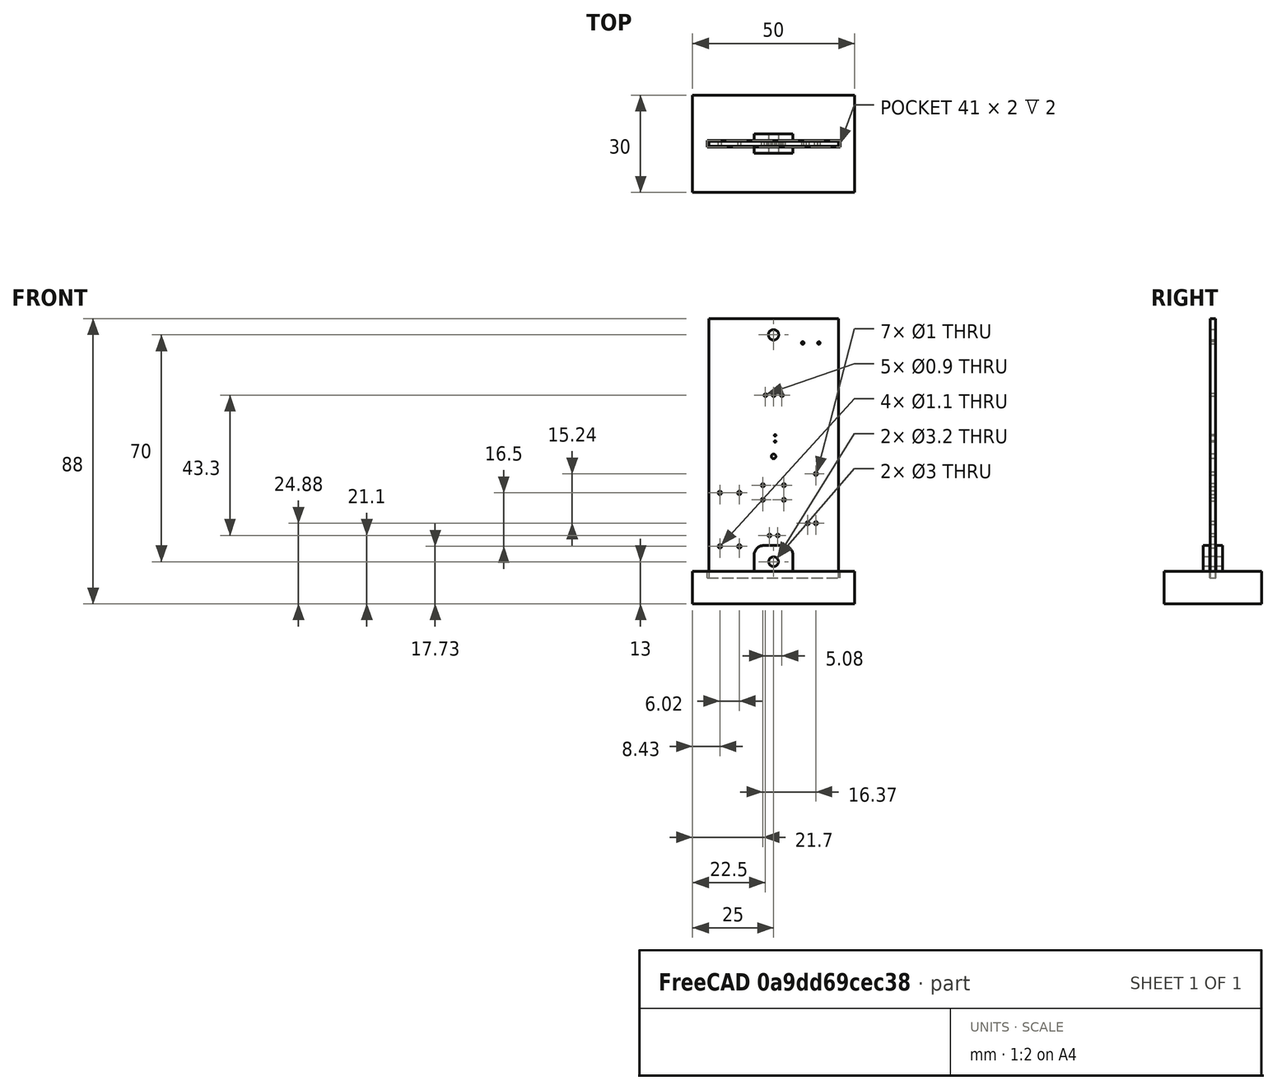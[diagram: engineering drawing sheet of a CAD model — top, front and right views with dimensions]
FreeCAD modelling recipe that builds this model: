
FCSTD DOCUMENT  (FreeCAD 0.15R4671 (Git))
Label: Sense_Beam_PCB_Holder
License: All rights reserved
LicenseURL: http://en.wikipedia.org/wiki/All_rights_reserved
objects: Part::Box×4, Part::MultiFuse×2, Part::Cut×2, Part::Feature×2, Part::Cylinder×1, Part::Fillet×1
note: 12 computed .brp shape members not serialized (recipe doc carries the construction recipe); baked Part::Feature solids carry a one-line shape summary decoded from their .brp

FEATURE [Part::Box] Box  label="Base1"
  Height = 10
  Length = 50
  Width = 30
FEATURE [Part::Box] Box001  label="Base2"
  Height = 18
  Length = 12
  Placement = pos=(19,12,0) rot=(0,0,1;0rad)
  Width = 6
FEATURE [Part::Cylinder] Cylinder  label="Cut002"
  Angle = 360
  Height = 10
  Placement = pos=(25,20,13) rot=(1,0,0;1.5708rad)
  Radius = 1.5
FEATURE [Part::Box] Box002  label="Cut2"
  Height = 9.5
  Length = 12
  Placement = pos=(19,14,10) rot=(0,0,1;0rad)
  Width = 2
FEATURE [Part::MultiFuse] Fusion
  Shapes = -> [Box,Box001]
FEATURE [Part::MultiFuse] Fusion001
  Shapes = -> [Box002,Cylinder]
FEATURE [Part::Cut] Cut  label="Cut003"
  Base = -> Fusion
  Tool = -> Fusion001
FEATURE [Part::Feature] Part__Feature  label="Board_Geoms"
  Placement = pos=(-95,14.2,158) rot=(1,0,0;1.5708rad)
  shape: bbox 40 x 1.6 x 80 mm, 29 faces (baked)
FEATURE [Part::Feature] Part__Feature001  label="senseBeRx_rev1"
FEATURE [Part::Box] Box003  label="Base3"
  Height = 2
  Length = 41
  Placement = pos=(4.5,14,8) rot=(0,0,1;0rad)
  Width = 2
FEATURE [Part::Cut] Cut001
  Base = -> Cut
  Tool = -> Box003
FEATURE [Part::Fillet] Fillet
  Base = -> Cut001
  Edges = 4 edges r=3: [Edge30,Edge42,Edge48,Edge51]
